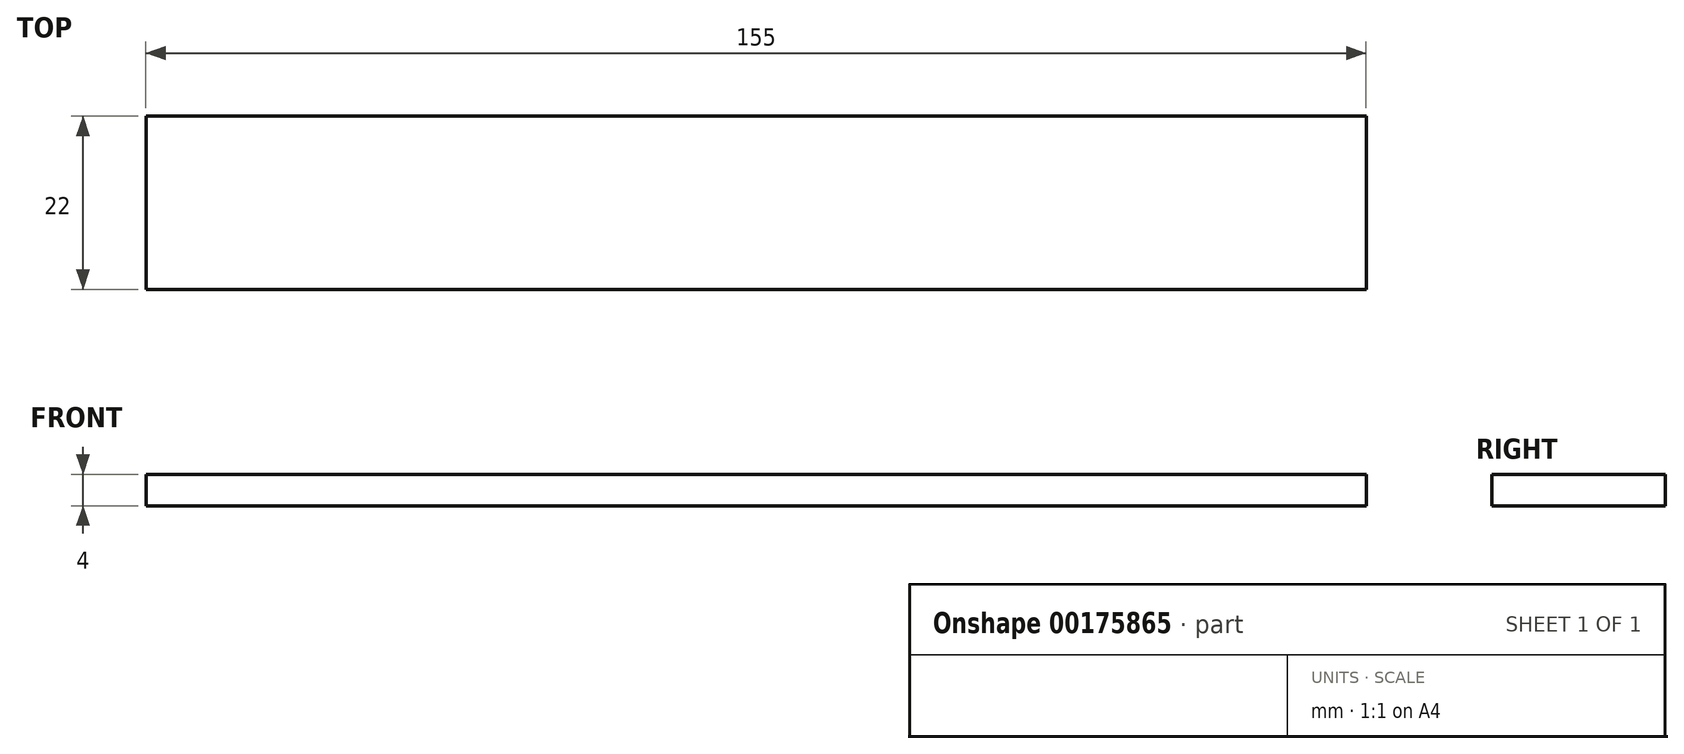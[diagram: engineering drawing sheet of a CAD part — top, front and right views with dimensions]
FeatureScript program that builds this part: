
annotation { "Feature Type Name" : "Feature", "Feature Type Description" : "" }
export const myFeature = defineFeature(function(context is Context, id is Id, definition is map)
    precondition{}
    {
        {
            var Q0;
            Q0=qCreatedBy(makeId("Top.planeOp"),FACE);
            var sketch = newSketch(context, id + "F0", { "sketchPlane" : qUnion([Q0])});
            skLineSegment(sketch, "E0.bottom", {"start": v(-120.49, -13.6) * mm, "end": v(34.51, -13.6) * mm});
            skLineSegment(sketch, "E0.top", {"start": v(-120.49, -35.6) * mm, "end": v(34.51, -35.6) * mm});
            skLineSegment(sketch, "E0.left", {"start": v(-120.49, -13.6) * mm, "end": v(-120.49, -35.6) * mm});
            skLineSegment(sketch, "E0.right", {"start": v(34.51, -13.6) * mm, "end": v(34.51, -35.6) * mm});
            skSolve(sketch);
        }
        {
            var Q0;
            Q0=qSketchRegion(id+"F0",true);
            extrude(context, id + "F1", {"entities" : qUnion([Q0]), "depth" : 4 * mm});
        }
    });
